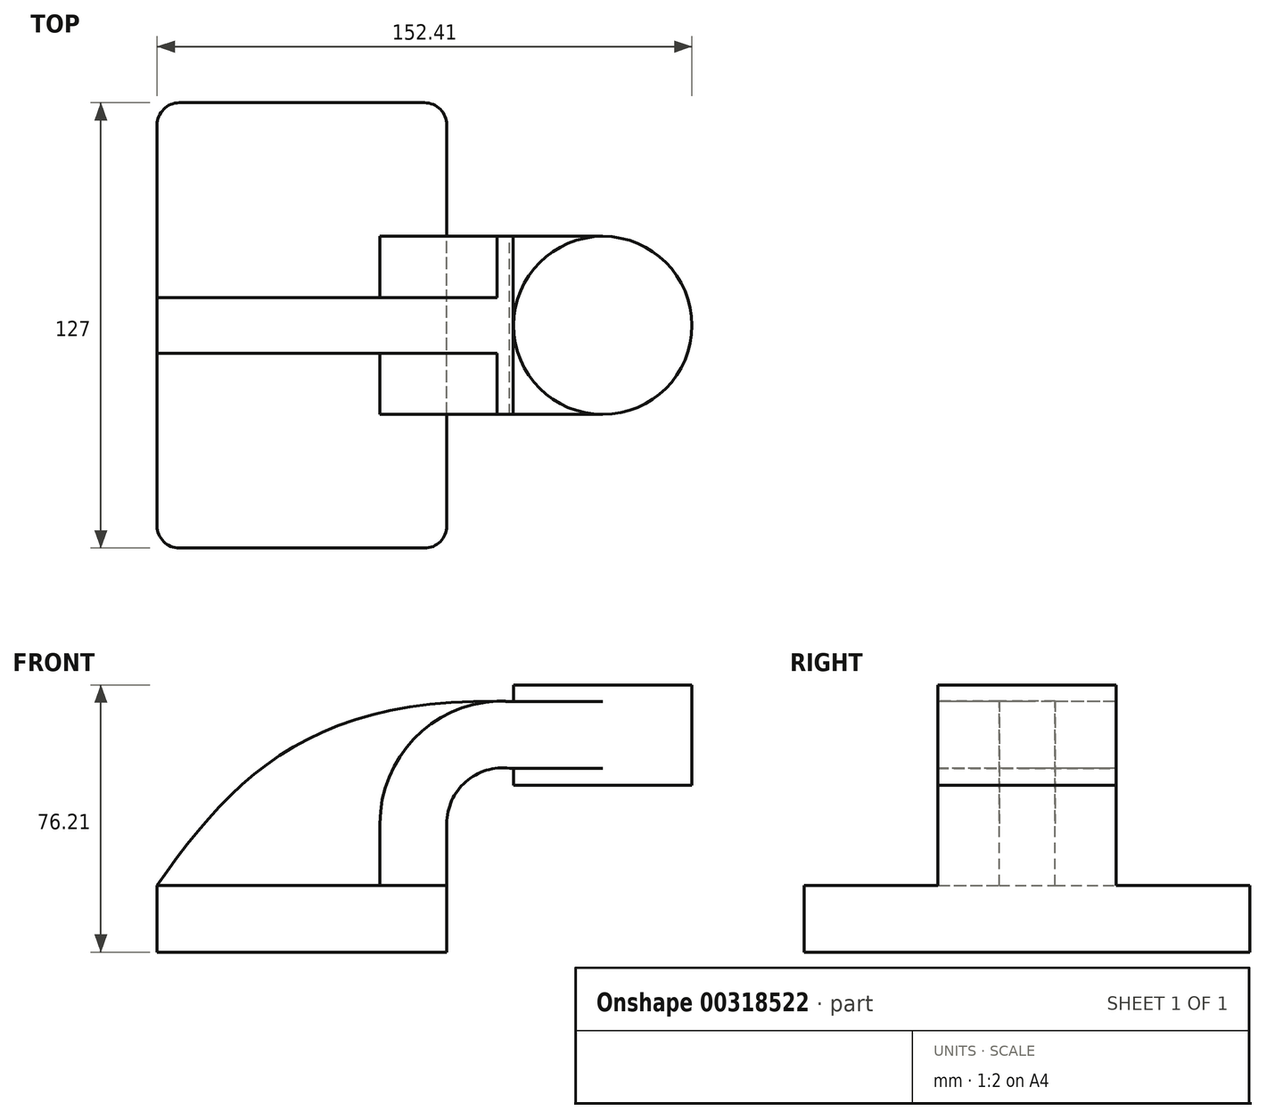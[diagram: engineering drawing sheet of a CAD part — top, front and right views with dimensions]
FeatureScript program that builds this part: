
annotation { "Feature Type Name" : "Feature", "Feature Type Description" : "" }
export const myFeature = defineFeature(function(context is Context, id is Id, definition is map)
    precondition{}
    {
        {
            var Q0;
            Q0=qCreatedBy(makeId("Front.planeOp"),FACE);
            var sketch = newSketch(context, id + "F0", { "sketchPlane" : qUnion([Q0])});
            skLineSegment(sketch, "E0.bottom", {"start": v(-41.28, 9.52) * mm, "end": v(41.27, 9.53) * mm});
            skLineSegment(sketch, "E0.top", {"start": v(-41.27, -9.53) * mm, "end": v(41.28, -9.53) * mm});
            skLineSegment(sketch, "E0.left", {"start": v(-41.28, 9.52) * mm, "end": v(-41.27, -9.53) * mm});
            skLineSegment(sketch, "E0.right", {"start": v(41.28, 9.53) * mm, "end": v(41.28, -9.52) * mm});
            skPoint(sketch, "E0.middle", {"position": v(0, 0) * mm});
            skLineSegment(sketch, "E1.bottom", {"start": v(60.32, 66.68) * mm, "end": v(111.12, 66.68) * mm});
            skLineSegment(sketch, "E1.top", {"start": v(60.32, 38.1) * mm, "end": v(111.12, 38.1) * mm});
            skLineSegment(sketch, "E1.left", {"start": v(60.32, 66.68) * mm, "end": v(60.32, 38.1) * mm});
            skLineSegment(sketch, "E1.right", {"start": v(111.12, 66.68) * mm, "end": v(111.12, 38.1) * mm});
            skPoint(sketch, "E1.middle", {"position": v(85.72, 52.39) * mm});
            skLineSegment(sketch, "E2", {"start": v(41.27, 9.53) * mm, "end": v(41.27, 27.13) * mm});
            skArc(sketch, "E3", {"start": v(59.2, 42.88) * mm, "mid": v(46.68, 39.06) * mm, "end": v(41.27, 27.13) * mm});
            skLineSegment(sketch, "E4", {"start": v(59.2, 42.88) * mm, "end": v(85.72, 42.88) * mm});
            skLineSegment(sketch, "E5.0", {"start": v(60.2, 61.93) * mm, "end": v(85.72, 61.93) * mm});
            skArc(sketch, "E5.1", {"start": v(60.2, 61.93) * mm, "mid": v(33.56, 52.88) * mm, "end": v(22.22, 27.13) * mm});
            skLineSegment(sketch, "E5.2", {"start": v(22.22, 9.53) * mm, "end": v(22.22, 27.13) * mm});
            skLineSegment(sketch, "E6", {"start": v(85.72, 38.1) * mm, "end": v(85.72, 66.68) * mm});
            skFitSpline(sketch, "E7", {"points": [v(-41.28, 9.52) * mm, v(60.2, 61.93) * mm], "startDerivative": vector(67.65, 97.15) * mm, "endDerivative": vector(168.56, -5.48) * mm});
            skSolve(sketch);
        }
        {
            var Q0;
            Q0=makeQuery(id+"F0.imprint","IMPRINT",FACE,{"disambiguationData":[TD([[makeQuery(id+"F0.imprint","IMPRINT",EDGE,{"derivedFrom":sQuery(id+"F0.wireOp",EDGE,"E0.top")}),1.0]])]});
            extrude(context, id + "F1", {"entities" : qUnion([Q0]), "endBound" : BoundingType.SYMMETRIC, "depth" : 127 * mm});
        }
        {
            var Q0;
            {var subQ1=sQuery(id+"F0.wireOp",EDGE,"E2");Q0=makeQuery(id+"F0.imprint","IMPRINT",FACE,{"disambiguationData":[TD([[makeQuery(id+"F0.imprint","IMPRINT",EDGE,{"derivedFrom":subQ1}),1.0]])]});}
            extrude(context, id + "F2", {"entities" : qUnion([Q0]), "operationType" : NewBodyOperationType.ADD, "endBound" : BoundingType.SYMMETRIC, "depth" : 50.8 * mm});
        }
        {
            var Q0;
            {var subQ3=sQuery(id+"F0.wireOp",EDGE,"E5.2");Q0=makeQuery(id+"F0.imprint","IMPRINT",FACE,{"disambiguationData":[TD([[makeQuery(id+"F0.imprint","IMPRINT",EDGE,{"derivedFrom":subQ3}),1.0]])]});}
            extrude(context, id + "F3", {"entities" : qUnion([Q0]), "operationType" : NewBodyOperationType.ADD, "endBound" : BoundingType.SYMMETRIC, "depth" : 15.88 * mm});
        }
        {
            var Q0;
            {var subQ0=sQuery(id+"F0.wireOp",EDGE,"E5.0");var subQ1=sQuery(id+"F0.wireOp",EDGE,"E1.left");var subQ2=makeQuery(id+"F0.imprint","INTERSECT",VERTEX,{"derivedFrom":[subQ1,subQ0]});Q0=makeQuery(id+"F0.imprint","IMPRINT",FACE,{"disambiguationData":[TD([[makeQuery(id+"F0.imprint","IMPRINT",EDGE,{"disambiguationData":[TD([[subQ2,-1.0]])],"derivedFrom":subQ1}),1.0]])]});}
            extrude(context, id + "F4", {"entities" : qUnion([Q0]), "operationType" : NewBodyOperationType.ADD, "endBound" : BoundingType.SYMMETRIC, "depth" : 50.8 * mm});
        }
        {
            var Q0;
            {var subQ4=sQuery(id+"F0.wireOp",EDGE,"E1.right");Q0=makeQuery(id+"F0.imprint","IMPRINT",FACE,{"disambiguationData":[TD([[makeQuery(id+"F0.imprint","IMPRINT",EDGE,{"derivedFrom":subQ4}),-1.0]])]});}
            var Q1;
            Q1=sQuery(id+"F0.wireOp",EDGE,"E6");
            revolve(context, id + "F5", {"operationType" : NewBodyOperationType.ADD, "entities" : qUnion([Q0]), "axis" : qUnion([Q1]), "revolveType" : RevolveType.FULL});
        }
        {
            var Q0;
            Q0=makeQuery(id+"F1.opExtrude","CAP_EDGE",EDGE,{"disambiguationData":[OSD([sQuery(id+"F0.wireOp",EDGE,"E0.left")])],"isStart":false});
            var Q1;
            Q1=makeQuery(id+"F1.opExtrude","CAP_EDGE",EDGE,{"disambiguationData":[OSD([sQuery(id+"F0.wireOp",EDGE,"E0.right")])],"isStart":false});
            var Q2;
            Q2=makeQuery(id+"F1.opExtrude","CAP_EDGE",EDGE,{"disambiguationData":[OSD([sQuery(id+"F0.wireOp",EDGE,"E0.left")])],"isStart":true});
            var Q3;
            Q3=makeQuery(id+"F1.opExtrude","CAP_EDGE",EDGE,{"disambiguationData":[OSD([sQuery(id+"F0.wireOp",EDGE,"E0.right")])],"isStart":true});
            fillet(context, id + "F6", {"entities" : qUnion([Q0, Q1, Q2, Q3]), "radius" : 6.35 * mm, "tangentPropagation" : true, "allowEdgeOverflow" : false});
        }
    });
